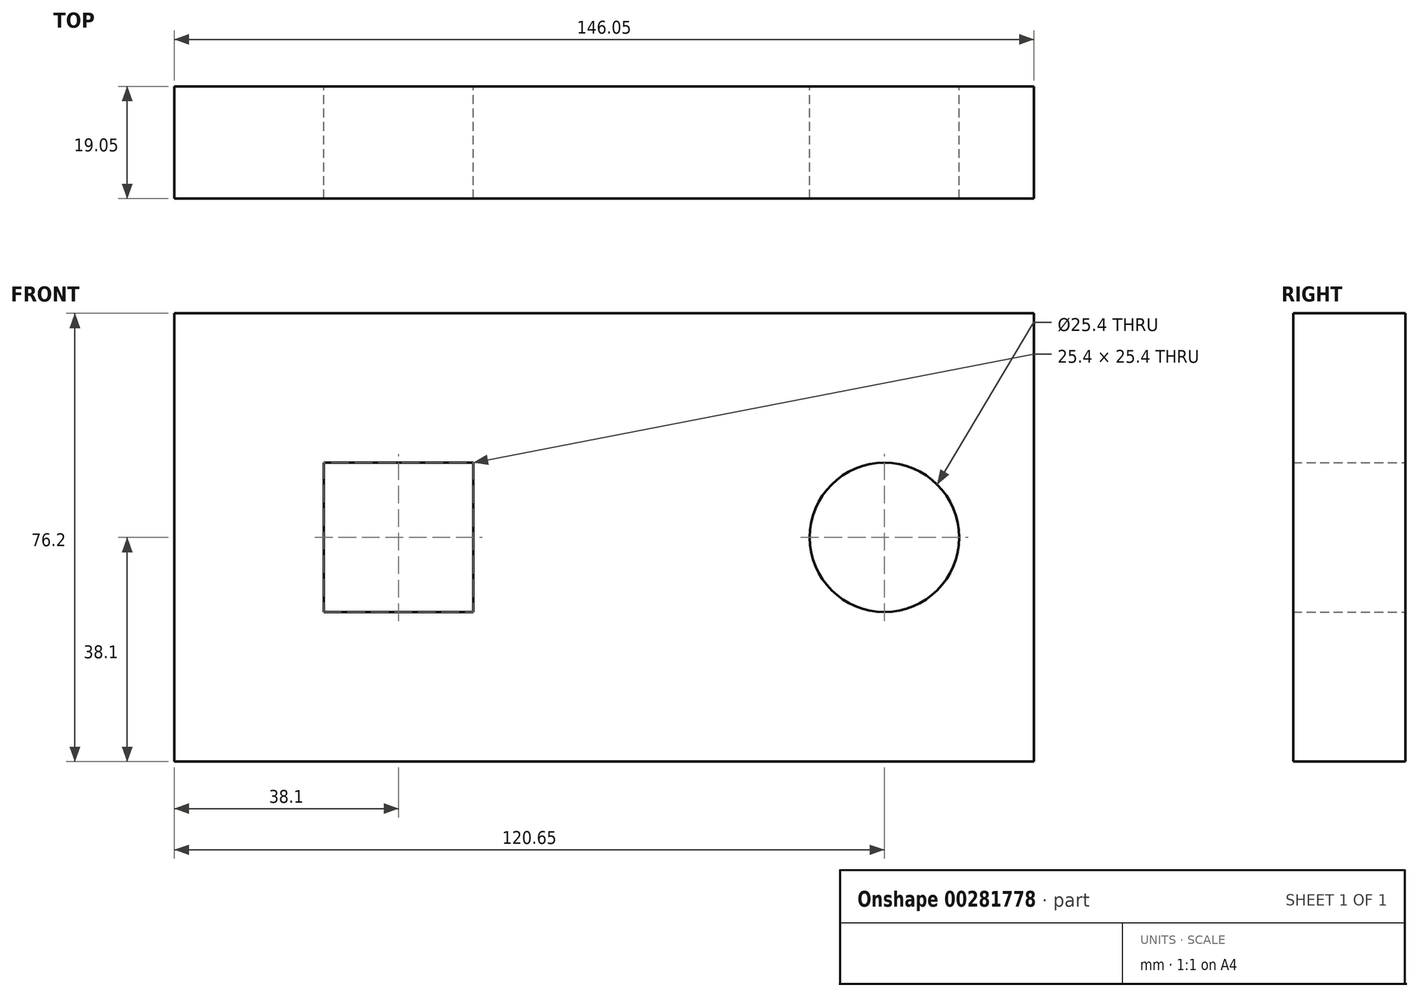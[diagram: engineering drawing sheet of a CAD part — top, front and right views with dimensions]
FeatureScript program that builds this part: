
annotation { "Feature Type Name" : "Feature", "Feature Type Description" : "" }
export const myFeature = defineFeature(function(context is Context, id is Id, definition is map)
    precondition{}
    {
        {
            var Q0;
            Q0=qCreatedBy(makeId("Front.planeOp"),FACE);
            var sketch = newSketch(context, id + "F0", { "sketchPlane" : qUnion([Q0])});
            skLineSegment(sketch, "E0.bottom", {"start": v(0, 0) * mm, "end": v(-146.05, 0) * mm});
            skLineSegment(sketch, "E0.top", {"start": v(0, 76.2) * mm, "end": v(-146.05, 76.2) * mm});
            skLineSegment(sketch, "E0.left", {"start": v(0, 0) * mm, "end": v(0, 76.2) * mm});
            skLineSegment(sketch, "E0.right", {"start": v(-146.05, 0) * mm, "end": v(-146.05, 76.2) * mm});
            skCircle(sketch, "E1", {"center": v(-25.4, 38.1) * mm, "radius": 12.7 * mm});
            skLineSegment(sketch, "E2.bottom", {"start": v(-120.65, 50.8) * mm, "end": v(-95.25, 50.8) * mm});
            skLineSegment(sketch, "E2.top", {"start": v(-120.65, 25.4) * mm, "end": v(-95.25, 25.4) * mm});
            skLineSegment(sketch, "E2.left", {"start": v(-120.65, 50.8) * mm, "end": v(-120.65, 25.4) * mm});
            skLineSegment(sketch, "E2.right", {"start": v(-95.25, 50.8) * mm, "end": v(-95.25, 25.4) * mm});
            skSolve(sketch);
        }
        {
            var Q0;
            Q0 = qSketchRegion(id + "F0", true);
            extrude(context, id + "F1", {"entities" : qUnion([Q0]), "depth" : 19.05 * mm});
        }
    });
